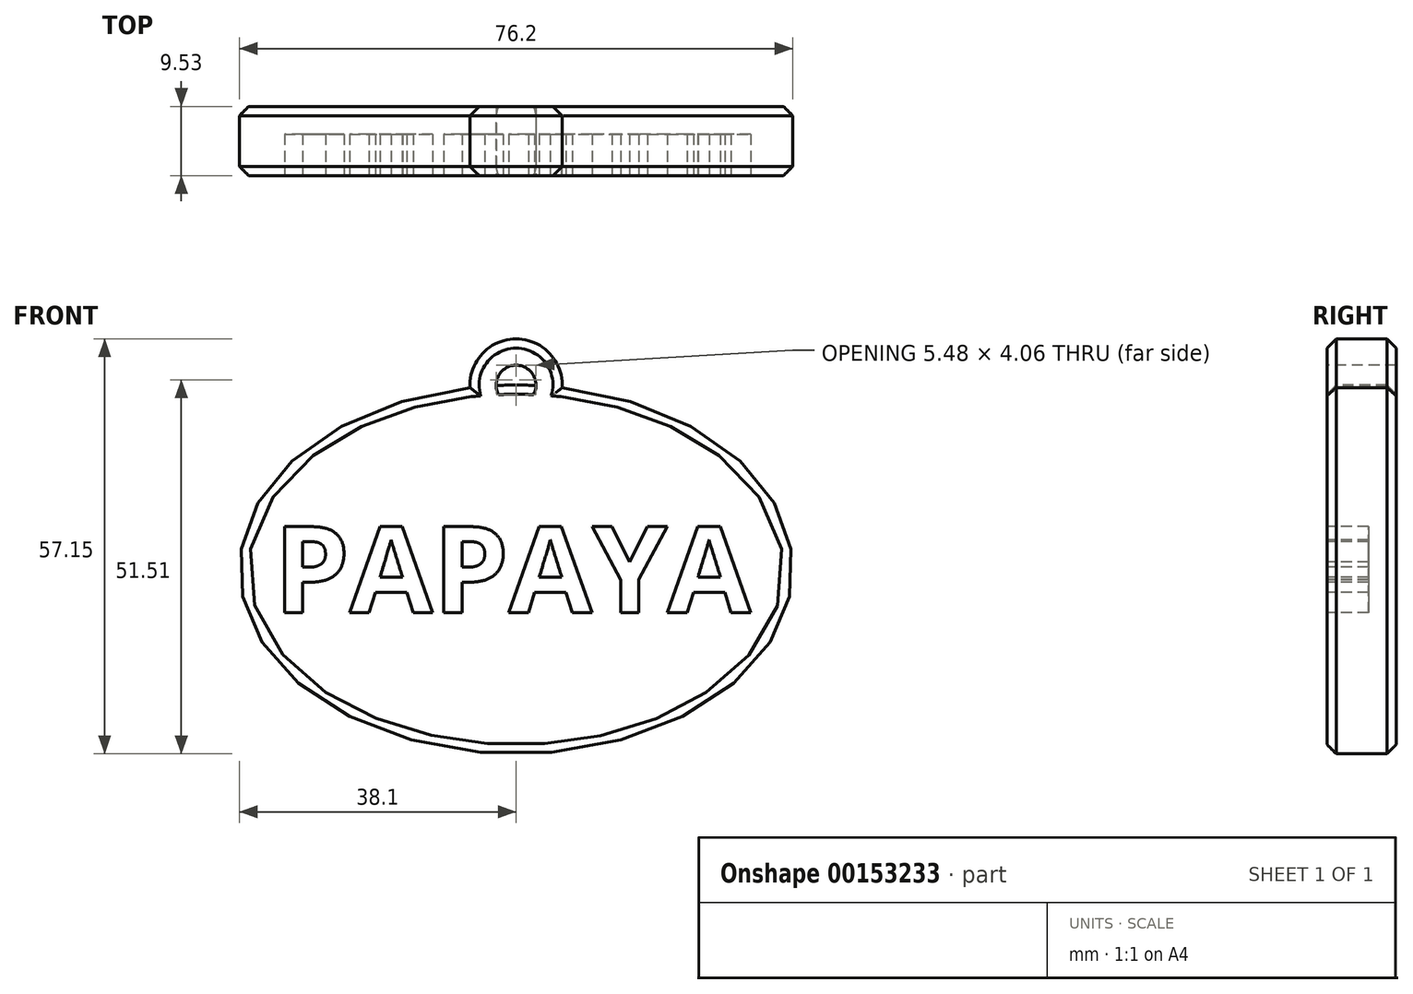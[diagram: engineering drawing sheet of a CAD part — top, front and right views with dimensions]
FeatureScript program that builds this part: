
annotation { "Feature Type Name" : "Feature", "Feature Type Description" : "" }
export const myFeature = defineFeature(function(context is Context, id is Id, definition is map)
    precondition{}
    {
        {
            var Q0;
            Q0=qCreatedBy(makeId("Front.planeOp"),FACE);
            var sketch = newSketch(context, id + "F0", { "sketchPlane" : qUnion([Q0])});
            skEllipse(sketch, "E0", {"center": v(0, 0) * mm, "majorRadius": 25.4 * mm, "minorRadius": 38.1 * mm, "majorAxis": v(0, 1)});
            skSolve(sketch);
        }
        {
            var Q0;
            Q0=makeQuery(id+"F0.imprint","IMPRINT",FACE,{"disambiguationData":[TD([[makeQuery(id+"F0.imprint","IMPRINT",EDGE,{"derivedFrom":sQuery(id+"F0.wireOp",EDGE,"E0")}),1.0]])]});
            extrude(context, id + "F1", {"entities" : qUnion([Q0]), "depth" : 9.52 * mm});
        }
        {
            var Q0;
            Q0=makeQuery(id+"F1.opExtrude","CAP_FACE",FACE,{"disambiguationData":[OSD([sQuery(id+"F0.wireOp",EDGE,"E0")])],"isStart":false});
            var sketch = newSketch(context, id + "F2", { "sketchPlane" : qUnion([Q0])});
            skText(sketch, "E1", { "text": "PAPAYA", "fontName": "OpenSans-Bold.ttf"});
            const initialGuessF2  = {"E1": [-0.0334, -0.00599, 1, 0, 0.01198]};
            skSetInitialGuess(sketch, initialGuessF2);
            skSolve(sketch);
        }
        {
            var Q0;
            Q0 = qSketchRegion(id + "F2", true);
            extrude(context, id + "F3", {"entities" : qUnion([Q0]), "operationType" : NewBodyOperationType.REMOVE, "oppositeDirection" : true, "depth" : 5.7 * mm});
        }
        {
            var Q0;
            {var subQ0=sQuery(id+"F0.wireOp",EDGE,"E0");Q0=makeQuery(id+"F3.boolean.opBoolean","SPLIT",FACE,{"disambiguationData":[TD([makeQuery(id+"F1.opExtrude","SWEPT_FACE",FACE,{"disambiguationData":[OSD([subQ0])]})])],"derivedFrom":makeQuery(id+"F1.opExtrude","CAP_FACE",FACE,{"disambiguationData":[OSD([subQ0])],"isStart":false})});}
            var sketch = newSketch(context, id + "F4", { "sketchPlane" : qUnion([Q0])});
            skCircle(sketch, "E2", {"center": v(0, 25.4) * mm, "radius": 6.35 * mm});
            skCircle(sketch, "E3", {"center": v(0, 25.4) * mm, "radius": 2.74 * mm});
            skSolve(sketch);
        }
        {
            var Q0;
            {var subQ0=sQuery(id+"F0.wireOp",EDGE,"E0");var subQ1=sQuery(id+"F4.wireOp",EDGE,"E2");Q0=makeQuery(id+"FQQeIBTsFYGSEc3_1.boolean.opBoolean","SPLIT",EDGE,{"disambiguationData":[TD([makeQuery(id+"FQQeIBTsFYGSEc3_1.opExtrude","SWEPT_FACE",FACE,{"disambiguationData":[OSD([subQ1])]})])],"derivedFrom":makeQuery(id+"F1.opExtrude","CAP_EDGE",EDGE,{"disambiguationData":[OSD([subQ0])],"isStart":false})});}
            chamfer(context, id + "F5", {"entities" : qUnion([Q0]), "width" : 1.27 * mm, "tangentPropagation" : true});
        }
        {
            var Q0;
            {var subQ0=sQuery(id+"F0.wireOp",EDGE,"E0");Q0=makeQuery(id+"FQQeIBTsFYGSEc3_1.boolean.opBoolean","SPLIT",EDGE,{"disambiguationData":[TD([makeQuery(id+"FQQeIBTsFYGSEc3_1.opExtrude","SWEPT_FACE",FACE,{"disambiguationData":[OSD([sQuery(id+"F4.wireOp",EDGE,"E2")])]})])],"derivedFrom":makeQuery(id+"F1.opExtrude","CAP_EDGE",EDGE,{"disambiguationData":[OSD([subQ0])],"isStart":true})});}
            chamfer(context, id + "F6", {"entities" : qUnion([Q0]), "width" : 1.27 * mm, "tangentPropagation" : true});
        }
        {
            var Q0;
            {var subQ0=sQuery(id+"F4.wireOp",EDGE,"E2");var subQ1=makeQuery(id+"F1.opExtrude","CAP_EDGE",EDGE,{"disambiguationData":[OSD([sQuery(id+"F0.wireOp",EDGE,"E0")])],"isStart":false});var subQ2=makeQuery(id+"F4.imprint","INTERSECT",VERTEX,{"disambiguationData":[OD(0.0)],"derivedFrom":[subQ1,subQ0]});Q0=makeQuery(id+"F4.imprint","IMPRINT",FACE,{"disambiguationData":[TD([[makeQuery(id+"F4.imprint","IMPRINT",EDGE,{"disambiguationData":[TD([[subQ2,-1.0]])],"derivedFrom":subQ0}),1.0]])]});}
            var Q1;
            {var subQ0=sQuery(id+"F4.wireOp",EDGE,"E2");var subQ1=makeQuery(id+"F1.opExtrude","CAP_EDGE",EDGE,{"disambiguationData":[OSD([sQuery(id+"F0.wireOp",EDGE,"E0")])],"isStart":false});var subQ2=makeQuery(id+"F4.imprint","INTERSECT",VERTEX,{"disambiguationData":[OD(0.0)],"derivedFrom":[subQ1,subQ0]});Q1=makeQuery(id+"F4.imprint","IMPRINT",FACE,{"disambiguationData":[TD([[makeQuery(id+"F4.imprint","IMPRINT",EDGE,{"disambiguationData":[TD([[subQ2,1.0]])],"derivedFrom":subQ0}),1.0]])]});}
            var Q2;
            Q2=makeQuery(id+"F1.opExtrude","CAP_FACE",FACE,{"disambiguationData":[OSD([sQuery(id+"F0.wireOp",EDGE,"E0")])],"isStart":true});
            extrude(context, id + "F7", {"entities" : qUnion([Q0, Q1]), "operationType" : NewBodyOperationType.ADD, "endBound" : BoundingType.UP_TO_SURFACE, "oppositeDirection" : true, "endBoundEntityFace" : qUnion([Q2]), "depth" : 25.4 * mm});
        }
        {
            var Q0;
            Q0=makeQuery(id+"F7.opExtrude","CAP_EDGE",EDGE,{"disambiguationData":[OSD([sQuery(id+"F4.wireOp",EDGE,"E2")])],"isStart":true});
            var Q1;
            Q1=makeQuery(id+"F7.opExtrude","CAP_EDGE",EDGE,{"disambiguationData":[OSD([sQuery(id+"F4.wireOp",EDGE,"E2")])],"isStart":false});
            chamfer(context, id + "F8", {"entities" : qUnion([Q0, Q1]), "width" : 1.27 * mm, "tangentPropagation" : true});
        }
    });
